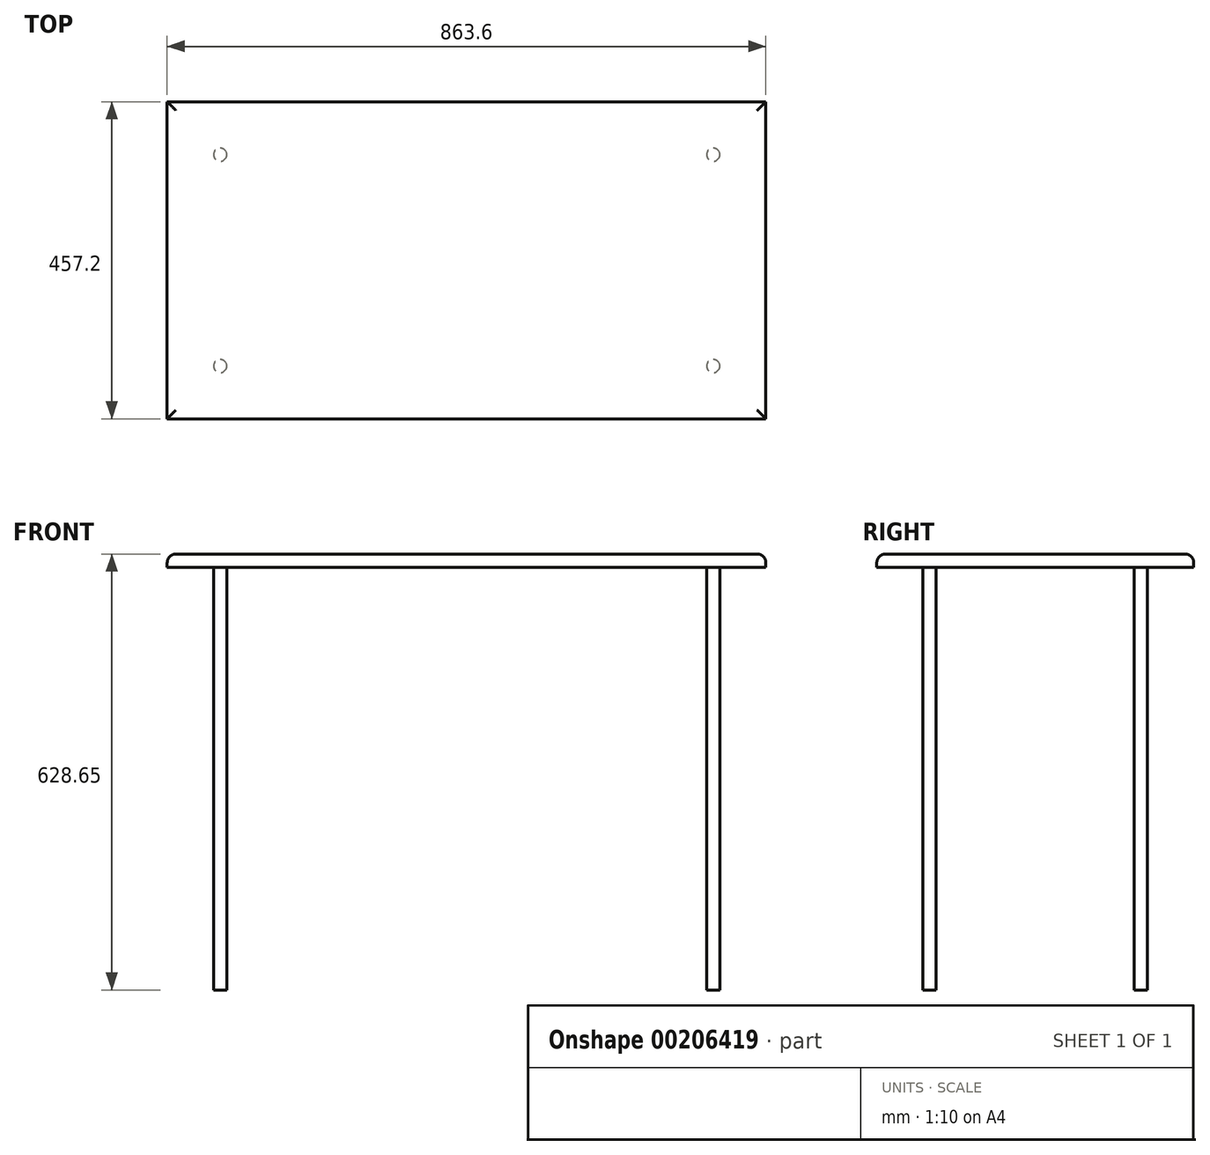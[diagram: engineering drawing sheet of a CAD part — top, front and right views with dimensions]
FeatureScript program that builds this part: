
annotation { "Feature Type Name" : "Feature", "Feature Type Description" : "" }
export const myFeature = defineFeature(function(context is Context, id is Id, definition is map)
    precondition{}
    {
        {
            var Q0;
            Q0=qCreatedBy(makeId("Top.planeOp"),FACE);
            var sketch = newSketch(context, id + "F0", { "sketchPlane" : qUnion([Q0])});
            skCircle(sketch, "E0", {"center": v(9.93, 11.34) * mm, "radius": 9.53 * mm});
            skCircle(sketch, "E1.0.1.0", {"center": v(9.93, 316.14) * mm, "radius": 9.53 * mm});
            skCircle(sketch, "E1.1.0.0", {"center": v(721.13, 11.34) * mm, "radius": 9.53 * mm});
            skCircle(sketch, "E1.1.1.0", {"center": v(721.13, 316.14) * mm, "radius": 9.53 * mm});
            skLineSegment(sketch, "E1.direction1", {"start": v(9.93, 11.34) * mm, "end": v(721.13, 11.34) * mm, "construction": true});
            skLineSegment(sketch, "E1.direction2", {"start": v(9.93, 11.34) * mm, "end": v(9.93, 316.14) * mm, "construction": true});
            skSolve(sketch);
        }
        {
            var Q0;
            Q0 = qSketchRegion(id + "F0", true);
            extrude(context, id + "F1", {"entities" : qUnion([Q0]), "depth" : 609.6 * mm});
        }
        {
            var Q0;
            Q0=makeQuery(id+"F1.opExtrude","CAP_FACE",FACE,{"disambiguationData":[OSD([sQuery(id+"F0.wireOp",EDGE,"E0")])],"isStart":false});
            var sketch = newSketch(context, id + "F2", { "sketchPlane" : qUnion([Q0])});
            skLineSegment(sketch, "E2.bottom", {"start": v(-66.5, -64.63) * mm, "end": v(797.1, -64.63) * mm});
            skLineSegment(sketch, "E2.top", {"start": v(-66.5, 392.57) * mm, "end": v(797.1, 392.57) * mm});
            skLineSegment(sketch, "E2.left", {"start": v(-66.5, -64.63) * mm, "end": v(-66.5, 392.57) * mm});
            skLineSegment(sketch, "E2.right", {"start": v(797.1, -64.63) * mm, "end": v(797.1, 392.57) * mm});
            skSolve(sketch);
        }
        {
            var Q0;
            Q0=makeQuery(id+"F2.imprint","IMPRINT",FACE,{"disambiguationData":[TD([[makeQuery(id+"F2.imprint","IMPRINT",EDGE,{"derivedFrom":sQuery(id+"F2.wireOp",EDGE,"E2.bottom")}),1.0]])]});
            var Q1;
            Q1=makeQuery(id+"F2.imprint","IMPRINT",FACE,{"disambiguationData":[TD([[makeQuery(id+"F2.imprint","IMPRINT",EDGE,{"derivedFrom":makeQuery(id+"F1.opExtrude","CAP_EDGE",EDGE,{"disambiguationData":[OSD([sQuery(id+"F0.wireOp",EDGE,"E0")])],"isStart":false})}),1.0]])]});
            extrude(context, id + "F3", {"entities" : qUnion([Q0, Q1]), "operationType" : NewBodyOperationType.ADD, "depth" : 19.05 * mm});
        }
        {
            var Q0;
            Q0=makeQuery(id+"F3.opExtrude","CAP_FACE",FACE,{"disambiguationData":[OSD([sQuery(id+"F2.wireOp",EDGE,"E2.bottom"),sQuery(id+"F2.wireOp",EDGE,"E2.top"),sQuery(id+"F2.wireOp",EDGE,"E2.left"),sQuery(id+"F2.wireOp",EDGE,"E2.right")])],"isStart":false});
            fillet(context, id + "F4", {"entities" : qUnion([Q0]), "radius" : 12.7 * mm, "tangentPropagation" : true, "allowEdgeOverflow" : false});
        }
    });
